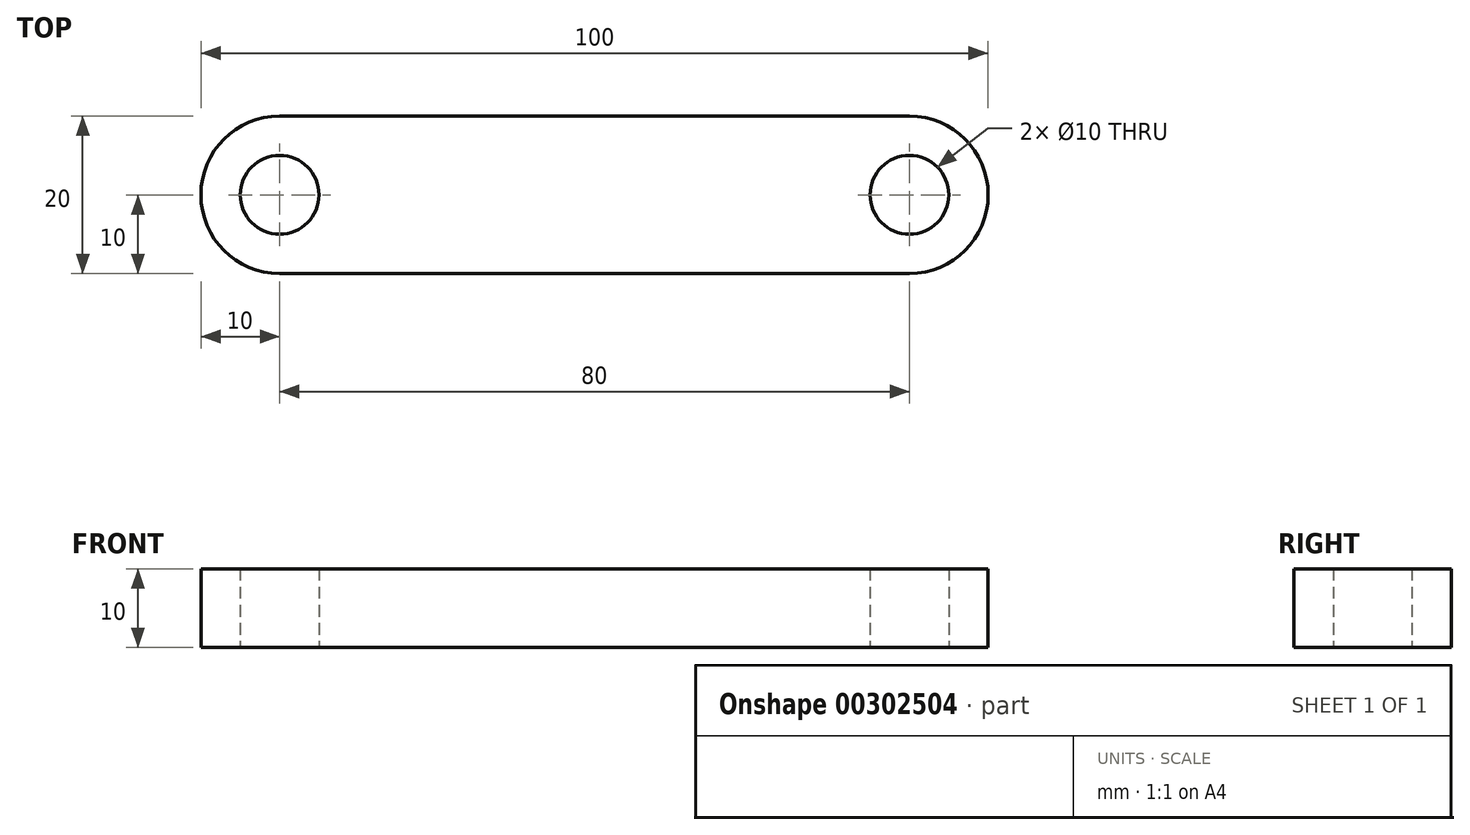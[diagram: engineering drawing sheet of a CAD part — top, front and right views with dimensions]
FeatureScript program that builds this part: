
annotation { "Feature Type Name" : "Feature", "Feature Type Description" : "" }
export const myFeature = defineFeature(function(context is Context, id is Id, definition is map)
    precondition{}
    {
        {
            var Q0;
            Q0=qCreatedBy(makeId("Top.planeOp"),FACE);
            var sketch = newSketch(context, id + "F0", { "sketchPlane" : qUnion([Q0])});
            skLineSegment(sketch, "E0", {"start": v(0, 0) * mm, "end": v(121.4, 0) * mm, "construction": true});
            skLineSegment(sketch, "E1", {"start": v(0, 0) * mm, "end": v(0, 0) * mm});
            skLineSegment(sketch, "E2", {"start": v(10, 10) * mm, "end": v(90, 10) * mm});
            skLineSegment(sketch, "E3", {"start": v(100, 0) * mm, "end": v(100, 0) * mm});
            skPoint(sketch, "E4.visualSharp", {"position": v(0, 10) * mm});
            skArc(sketch, "E4.filletArc", {"start": v(10, 10) * mm, "mid": v(2.93, 7.07) * mm, "end": v(0, 0) * mm});
            skPoint(sketch, "E5.visualSharp", {"position": v(100, 10) * mm});
            skArc(sketch, "E5.filletArc", {"start": v(100, 0) * mm, "mid": v(97.07, 7.07) * mm, "end": v(90, 10) * mm});
            skArc(sketch, "E6.MirrorCS", {"start": v(10, -10) * mm, "mid": v(2.93, -7.07) * mm, "end": v(0, 0) * mm});
            skArc(sketch, "E7.MirrorCS", {"start": v(100, 0) * mm, "mid": v(97.07, -7.07) * mm, "end": v(90, -10) * mm});
            skPoint(sketch, "E8.MirrorP", {"position": v(100, -10) * mm});
            skLineSegment(sketch, "E9.MirrorCS", {"start": v(10, -10) * mm, "end": v(90, -10) * mm});
            skPoint(sketch, "E10.MirrorP", {"position": v(0, -10) * mm});
            skCircle(sketch, "E11", {"center": v(10, 0) * mm, "radius": 5 * mm});
            skCircle(sketch, "E12", {"center": v(90, 0) * mm, "radius": 5 * mm});
            skSolve(sketch);
        }
        {
            var Q0;
            Q0 = qSketchRegion(id + "F0", true);
            extrude(context, id + "F1", {"entities" : qUnion([Q0]), "depth" : 10 * mm});
        }
    });
